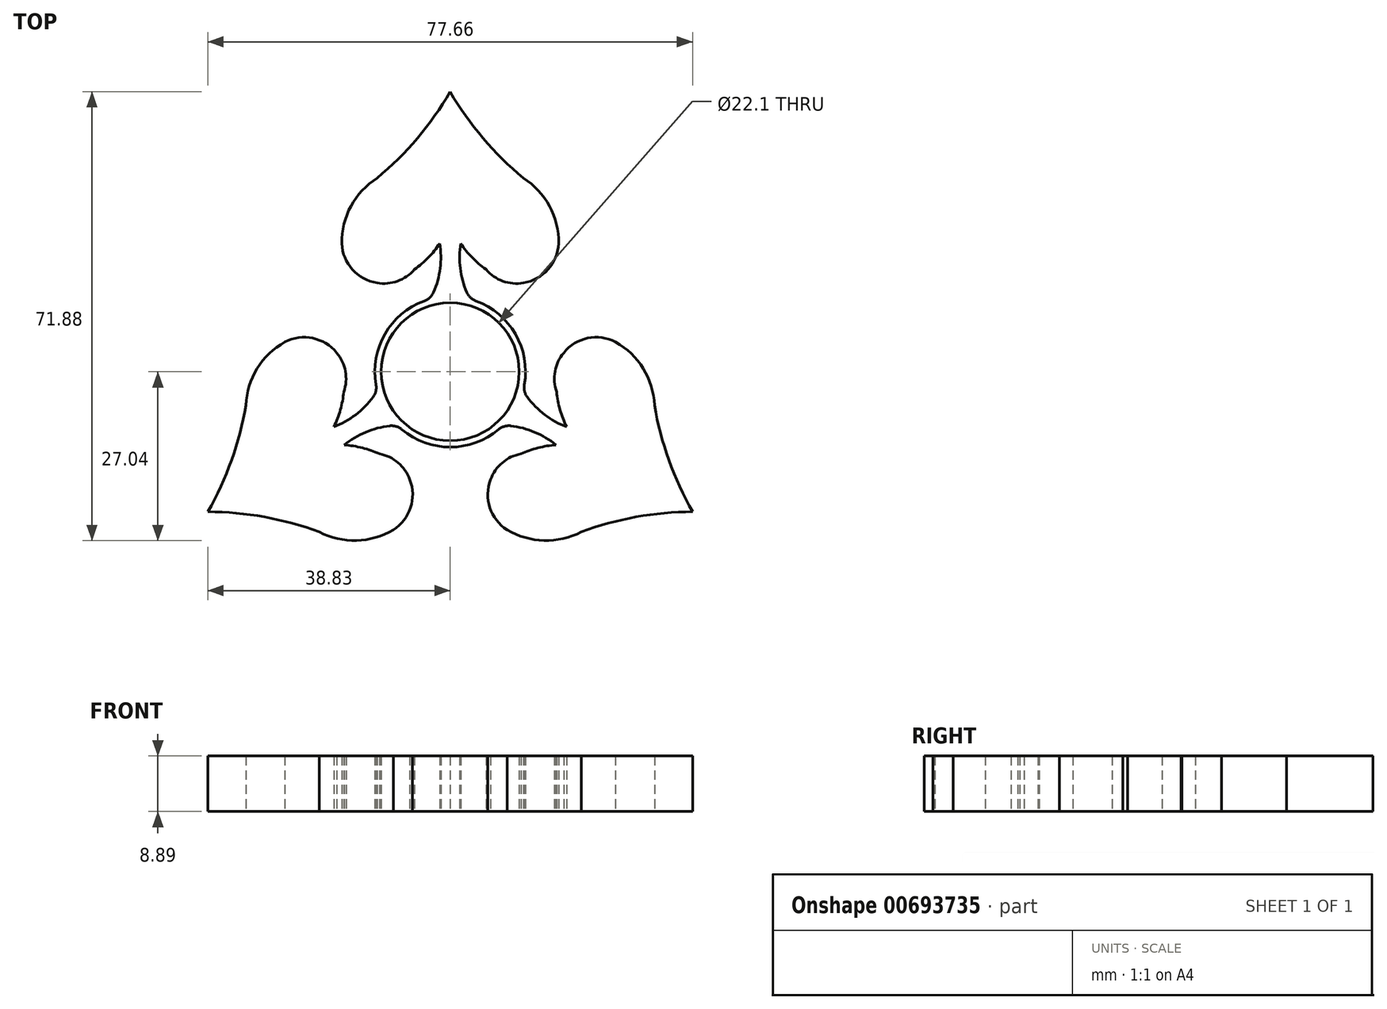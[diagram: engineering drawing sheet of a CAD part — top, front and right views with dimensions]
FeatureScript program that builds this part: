
annotation { "Feature Type Name" : "Feature", "Feature Type Description" : "" }
export const myFeature = defineFeature(function(context is Context, id is Id, definition is map)
    precondition{}
    {
        {
            var Q0;
            Q0=qCreatedBy(makeId("Top.planeOp"),FACE);
            var sketch = newSketch(context, id + "F0", { "sketchPlane" : qUnion([Q0])});
            skArc(sketch, "E0", {"start": v(0, 44.84) * mm, "mid": v(5.25, 37.41) * mm, "end": v(11.71, 31.02) * mm});
            skArc(sketch, "E1", {"start": v(17.37, 20.56) * mm, "mid": v(15.9, 26.52) * mm, "end": v(11.71, 31.02) * mm});
            skArc(sketch, "E2", {"start": v(11.71, 14.23) * mm, "mid": v(15.67, 16.38) * mm, "end": v(17.37, 20.56) * mm});
            skArc(sketch, "E3", {"start": v(5.73, 16.38) * mm, "mid": v(8.44, 14.5) * mm, "end": v(11.71, 14.23) * mm});
            skPoint(sketch, "E3.startSnap0", {"position": v(15.67, 16.38) * mm});
            skArc(sketch, "E4", {"start": v(1.69, 20.56) * mm, "mid": v(3.51, 18.28) * mm, "end": v(5.73, 16.38) * mm});
            skArc(sketch, "E5", {"start": v(1.69, 20.56) * mm, "mid": v(1.6, 16.56) * mm, "end": v(2.67, 12.7) * mm});
            skArc(sketch, "E6.MirrorCS", {"start": v(0, 44.84) * mm, "mid": v(-5.25, 37.41) * mm, "end": v(-11.71, 31.02) * mm});
            skArc(sketch, "E7.MirrorCS", {"start": v(-17.37, 20.56) * mm, "mid": v(-15.9, 26.52) * mm, "end": v(-11.71, 31.02) * mm});
            skArc(sketch, "E8.MirrorCS", {"start": v(-11.71, 14.23) * mm, "mid": v(-15.67, 16.38) * mm, "end": v(-17.37, 20.56) * mm});
            skArc(sketch, "E9.MirrorCS", {"start": v(-5.73, 16.38) * mm, "mid": v(-8.44, 14.5) * mm, "end": v(-11.71, 14.23) * mm});
            skArc(sketch, "E10.MirrorCS", {"start": v(-1.69, 20.56) * mm, "mid": v(-3.51, 18.28) * mm, "end": v(-5.73, 16.38) * mm});
            skArc(sketch, "E11.MirrorCS", {"start": v(-1.69, 20.56) * mm, "mid": v(-1.6, 16.56) * mm, "end": v(-2.67, 12.7) * mm});
            skArc(sketch, "E12.1.0", {"start": v(-18.65, -8.82) * mm, "mid": v(-15.15, -6.89) * mm, "end": v(-12.34, -4.04) * mm});
            skArc(sketch, "E12.1.3", {"start": v(-16.96, -11.74) * mm, "mid": v(-13.54, -9.67) * mm, "end": v(-9.67, -8.66) * mm});
            skArc(sketch, "E12.1.4", {"start": v(-16.96, -11.74) * mm, "mid": v(-14.07, -12.18) * mm, "end": v(-11.32, -13.16) * mm});
            skArc(sketch, "E12.1.5", {"start": v(-11.32, -13.16) * mm, "mid": v(-8.35, -14.56) * mm, "end": v(-6.47, -17.26) * mm});
            skArc(sketch, "E12.1.6", {"start": v(-6.47, -17.26) * mm, "mid": v(-6.35, -21.76) * mm, "end": v(-9.12, -25.32) * mm});
            skArc(sketch, "E12.1.7", {"start": v(-9.12, -25.32) * mm, "mid": v(-15.02, -27.03) * mm, "end": v(-21, -25.65) * mm});
            skArc(sketch, "E12.1.8", {"start": v(-38.83, -22.42) * mm, "mid": v(-29.77, -23.25) * mm, "end": v(-21, -25.65) * mm});
            skArc(sketch, "E12.1.9", {"start": v(-38.83, -22.42) * mm, "mid": v(-35.03, -14.16) * mm, "end": v(-32.72, -5.36) * mm});
            skArc(sketch, "E12.1.10", {"start": v(-26.49, 4.76) * mm, "mid": v(-30.92, 0.51) * mm, "end": v(-32.72, -5.36) * mm});
            skArc(sketch, "E12.1.11", {"start": v(-18.18, 3.03) * mm, "mid": v(-22.02, 5.38) * mm, "end": v(-26.49, 4.76) * mm});
            skArc(sketch, "E12.1.12", {"start": v(-17.05, -3.23) * mm, "mid": v(-16.78, 0.05) * mm, "end": v(-18.18, 3.03) * mm});
            skArc(sketch, "E12.1.13", {"start": v(-18.65, -8.82) * mm, "mid": v(-17.59, -6.1) * mm, "end": v(-17.05, -3.23) * mm});
            skArc(sketch, "E12.2.0", {"start": v(16.96, -11.74) * mm, "mid": v(13.54, -9.67) * mm, "end": v(9.67, -8.66) * mm});
            skArc(sketch, "E12.2.3", {"start": v(18.65, -8.82) * mm, "mid": v(15.15, -6.89) * mm, "end": v(12.34, -4.04) * mm});
            skArc(sketch, "E12.2.4", {"start": v(18.65, -8.82) * mm, "mid": v(17.59, -6.1) * mm, "end": v(17.05, -3.23) * mm});
            skArc(sketch, "E12.2.5", {"start": v(17.05, -3.23) * mm, "mid": v(16.78, 0.05) * mm, "end": v(18.18, 3.03) * mm});
            skArc(sketch, "E12.2.6", {"start": v(18.18, 3.03) * mm, "mid": v(22.02, 5.38) * mm, "end": v(26.49, 4.76) * mm});
            skArc(sketch, "E12.2.7", {"start": v(26.49, 4.76) * mm, "mid": v(30.92, 0.51) * mm, "end": v(32.72, -5.36) * mm});
            skArc(sketch, "E12.2.8", {"start": v(38.83, -22.42) * mm, "mid": v(35.03, -14.16) * mm, "end": v(32.72, -5.36) * mm});
            skArc(sketch, "E12.2.9", {"start": v(38.83, -22.42) * mm, "mid": v(29.77, -23.25) * mm, "end": v(21, -25.65) * mm});
            skArc(sketch, "E12.2.10", {"start": v(9.12, -25.32) * mm, "mid": v(15.02, -27.03) * mm, "end": v(21, -25.65) * mm});
            skArc(sketch, "E12.2.11", {"start": v(6.47, -17.26) * mm, "mid": v(6.35, -21.76) * mm, "end": v(9.12, -25.32) * mm});
            skArc(sketch, "E12.2.12", {"start": v(11.32, -13.16) * mm, "mid": v(8.35, -14.56) * mm, "end": v(6.47, -17.26) * mm});
            skArc(sketch, "E12.2.13", {"start": v(16.96, -11.74) * mm, "mid": v(14.07, -12.18) * mm, "end": v(11.32, -13.16) * mm});
            skCircle(sketch, "E13", {"center": v(0, 0) * mm, "radius": 11.05 * mm});
            skPoint(sketch, "E14.MirrorCS.end.orphan", {"position": v(0, 8.29) * mm});
            skPoint(sketch, "E14.MirrorCS.start.orphan", {"position": v(-5.73, 8.29) * mm});
            skArc(sketch, "E15", {"start": v(8.48, -8.58) * mm, "mid": v(11.79, 2.58) * mm, "end": v(4.13, 11.34) * mm});
            skArc(sketch, "E16", {"start": v(-8.48, -8.58) * mm, "mid": v(0, -12.07) * mm, "end": v(8.48, -8.58) * mm});
            skArc(sketch, "E17", {"start": v(-11.67, -3.05) * mm, "mid": v(-10.45, -6.03) * mm, "end": v(-8.48, -8.58) * mm});
            skArc(sketch, "E18", {"start": v(-4.13, 11.34) * mm, "mid": v(-10.69, 5.6) * mm, "end": v(-11.67, -3.05) * mm});
            skPoint(sketch, "E19.end.orphan", {"position": v(5.73, 8.29) * mm});
            skPoint(sketch, "E20.orphan", {"position": v(-4.31, -9.1) * mm});
            skPoint(sketch, "E21.orphan", {"position": v(-10.04, 0.82) * mm});
            skArc(sketch, "E22.filletArc", {"start": v(2.67, 12.7) * mm, "mid": v(3.26, 11.87) * mm, "end": v(4.13, 11.34) * mm});
            skPoint(sketch, "E23.visualSharp", {"position": v(-3.2, 11.63) * mm});
            skArc(sketch, "E23.filletArc", {"start": v(-4.13, 11.34) * mm, "mid": v(-3.26, 11.87) * mm, "end": v(-2.67, 12.7) * mm});
            skArc(sketch, "E24.1.0", {"start": v(-12.34, -4.04) * mm, "mid": v(-11.91, -3.12) * mm, "end": v(-11.88, -2.1) * mm});
            skArc(sketch, "E24.1.1", {"start": v(-7.75, -9.24) * mm, "mid": v(-8.65, -8.76) * mm, "end": v(-9.67, -8.66) * mm});
            skArc(sketch, "E24.2.0", {"start": v(9.67, -8.66) * mm, "mid": v(8.65, -8.76) * mm, "end": v(7.75, -9.24) * mm});
            skArc(sketch, "E24.2.1", {"start": v(11.88, -2.1) * mm, "mid": v(11.91, -3.12) * mm, "end": v(12.34, -4.04) * mm});
            skSolve(sketch);
        }
        {
            var Q0;
            {var subQ0=sQuery(id+"F0.wireOp",EDGE,"E6.MirrorCS");var subQ1=sQuery(id+"F0.wireOp",EDGE,"E0");var subQ2=makeQuery(id+"F0.imprint","INTERSECT",VERTEX,{"derivedFrom":[subQ1,subQ0]});Q0=makeQuery(id+"F0.imprint","IMPRINT",FACE,{"disambiguationData":[TD([[makeQuery(id+"F0.imprint","IMPRINT",EDGE,{"disambiguationData":[TD([[subQ2,-1.0]])],"derivedFrom":subQ1}),-1.0]])]});}
            var Q1;
            {var subQ0=sQuery(id+"F0.wireOp",EDGE,"E1");var subQ1=sQuery(id+"F0.wireOp",EDGE,"E0");var subQ2=makeQuery(id+"F0.imprint","INTERSECT",VERTEX,{"derivedFrom":[subQ1,subQ0]});Q1=makeQuery(id+"F0.imprint","IMPRINT",FACE,{"disambiguationData":[TD([[makeQuery(id+"F0.imprint","IMPRINT",EDGE,{"disambiguationData":[TD([[subQ2,1.0]])],"derivedFrom":subQ1}),1.0]])]});}
            var Q2;
            {var subQ0=sQuery(id+"F0.wireOp",EDGE,"E5");var subQ1=sQuery(id+"F0.wireOp",EDGE,"E4");var subQ2=makeQuery(id+"F0.imprint","INTERSECT",VERTEX,{"derivedFrom":[subQ1,subQ0]});Q2=makeQuery(id+"F0.imprint","IMPRINT",FACE,{"disambiguationData":[TD([[makeQuery(id+"F0.imprint","IMPRINT",EDGE,{"disambiguationData":[TD([[subQ2,-1.0]])],"derivedFrom":subQ1}),-1.0]])]});}
            var Q3;
            {var subQ0=sQuery(id+"F0.wireOp",EDGE,"E7.MirrorCS");var subQ1=sQuery(id+"F0.wireOp",EDGE,"E6.MirrorCS");var subQ2=makeQuery(id+"F0.imprint","INTERSECT",VERTEX,{"derivedFrom":[subQ1,subQ0]});Q3=makeQuery(id+"F0.imprint","IMPRINT",FACE,{"disambiguationData":[TD([[makeQuery(id+"F0.imprint","IMPRINT",EDGE,{"disambiguationData":[TD([[subQ2,1.0]])],"derivedFrom":subQ1}),-1.0]])]});}
            var Q4;
            {var subQ1=sQuery(id+"F0.wireOp",EDGE,"E8.MirrorCS");Q4=makeQuery(id+"F0.imprint","IMPRINT",FACE,{"disambiguationData":[TD([[makeQuery(id+"F0.imprint","IMPRINT",EDGE,{"derivedFrom":subQ1}),-1.0]])]});}
            var Q5;
            {var subQ0=sQuery(id+"F0.wireOp",EDGE,"E11.MirrorCS");var subQ1=sQuery(id+"F0.wireOp",EDGE,"E10.MirrorCS");var subQ2=makeQuery(id+"F0.imprint","INTERSECT",VERTEX,{"derivedFrom":[subQ1,subQ0]});Q5=makeQuery(id+"F0.imprint","IMPRINT",FACE,{"disambiguationData":[TD([[makeQuery(id+"F0.imprint","IMPRINT",EDGE,{"disambiguationData":[TD([[subQ2,-1.0]])],"derivedFrom":subQ1}),1.0]])]});}
            var Q6;
            {var subQ0=sQuery(id+"F0.wireOp",EDGE,"E12.1.13");var subQ1=sQuery(id+"F0.wireOp",EDGE,"E12.1.0");var subQ2=makeQuery(id+"F0.imprint","INTERSECT",VERTEX,{"derivedFrom":[subQ1,subQ0]});Q6=makeQuery(id+"F0.imprint","IMPRINT",FACE,{"disambiguationData":[TD([[makeQuery(id+"F0.imprint","IMPRINT",EDGE,{"disambiguationData":[TD([[subQ2,-1.0]])],"derivedFrom":subQ1}),1.0]])]});}
            var Q7;
            {var subQ0=sQuery(id+"F0.wireOp",EDGE,"E12.1.4");var subQ1=sQuery(id+"F0.wireOp",EDGE,"E12.1.3");var subQ2=makeQuery(id+"F0.imprint","INTERSECT",VERTEX,{"derivedFrom":[subQ1,subQ0]});Q7=makeQuery(id+"F0.imprint","IMPRINT",FACE,{"disambiguationData":[TD([[makeQuery(id+"F0.imprint","IMPRINT",EDGE,{"disambiguationData":[TD([[subQ2,-1.0]])],"derivedFrom":subQ1}),-1.0]])]});}
            var Q8;
            {var subQ4=sQuery(id+"F0.wireOp",EDGE,"E12.1.5");Q8=makeQuery(id+"F0.imprint","IMPRINT",FACE,{"disambiguationData":[TD([[makeQuery(id+"F0.imprint","IMPRINT",EDGE,{"derivedFrom":subQ4}),-1.0]])]});}
            var Q9;
            {var subQ0=sQuery(id+"F0.wireOp",EDGE,"E12.1.8");var subQ1=sQuery(id+"F0.wireOp",EDGE,"E12.1.7");var subQ2=makeQuery(id+"F0.imprint","INTERSECT",VERTEX,{"derivedFrom":[subQ1,subQ0]});Q9=makeQuery(id+"F0.imprint","IMPRINT",FACE,{"disambiguationData":[TD([[makeQuery(id+"F0.imprint","IMPRINT",EDGE,{"disambiguationData":[TD([[subQ2,1.0]])],"derivedFrom":subQ1}),1.0]])]});}
            var Q10;
            {var subQ0=sQuery(id+"F0.wireOp",EDGE,"E12.1.9");var subQ1=sQuery(id+"F0.wireOp",EDGE,"E12.1.8");var subQ2=makeQuery(id+"F0.imprint","INTERSECT",VERTEX,{"derivedFrom":[subQ1,subQ0]});Q10=makeQuery(id+"F0.imprint","IMPRINT",FACE,{"disambiguationData":[TD([[makeQuery(id+"F0.imprint","IMPRINT",EDGE,{"disambiguationData":[TD([[subQ2,-1.0]])],"derivedFrom":subQ1}),1.0]])]});}
            var Q11;
            {var subQ0=sQuery(id+"F0.wireOp",EDGE,"E12.1.10");var subQ1=sQuery(id+"F0.wireOp",EDGE,"E12.1.9");var subQ2=makeQuery(id+"F0.imprint","INTERSECT",VERTEX,{"derivedFrom":[subQ1,subQ0]});Q11=makeQuery(id+"F0.imprint","IMPRINT",FACE,{"disambiguationData":[TD([[makeQuery(id+"F0.imprint","IMPRINT",EDGE,{"disambiguationData":[TD([[subQ2,1.0]])],"derivedFrom":subQ1}),1.0]])]});}
            var Q12;
            {var subQ1=sQuery(id+"F0.wireOp",EDGE,"E12.1.11");Q12=makeQuery(id+"F0.imprint","IMPRINT",FACE,{"disambiguationData":[TD([[makeQuery(id+"F0.imprint","IMPRINT",EDGE,{"derivedFrom":subQ1}),1.0]])]});}
            var Q13;
            {var subQ0=sQuery(id+"F0.wireOp",EDGE,"E12.2.13");var subQ1=sQuery(id+"F0.wireOp",EDGE,"E12.2.0");var subQ2=makeQuery(id+"F0.imprint","INTERSECT",VERTEX,{"derivedFrom":[subQ1,subQ0]});Q13=makeQuery(id+"F0.imprint","IMPRINT",FACE,{"disambiguationData":[TD([[makeQuery(id+"F0.imprint","IMPRINT",EDGE,{"disambiguationData":[TD([[subQ2,-1.0]])],"derivedFrom":subQ1}),1.0]])]});}
            var Q14;
            {var subQ0=sQuery(id+"F0.wireOp",EDGE,"E12.2.4");var subQ1=sQuery(id+"F0.wireOp",EDGE,"E12.2.3");var subQ2=makeQuery(id+"F0.imprint","INTERSECT",VERTEX,{"derivedFrom":[subQ1,subQ0]});Q14=makeQuery(id+"F0.imprint","IMPRINT",FACE,{"disambiguationData":[TD([[makeQuery(id+"F0.imprint","IMPRINT",EDGE,{"disambiguationData":[TD([[subQ2,-1.0]])],"derivedFrom":subQ1}),-1.0]])]});}
            var Q15;
            {var subQ4=sQuery(id+"F0.wireOp",EDGE,"E12.2.5");Q15=makeQuery(id+"F0.imprint","IMPRINT",FACE,{"disambiguationData":[TD([[makeQuery(id+"F0.imprint","IMPRINT",EDGE,{"derivedFrom":subQ4}),-1.0]])]});}
            var Q16;
            {var subQ0=sQuery(id+"F0.wireOp",EDGE,"E12.2.8");var subQ1=sQuery(id+"F0.wireOp",EDGE,"E12.2.7");var subQ2=makeQuery(id+"F0.imprint","INTERSECT",VERTEX,{"derivedFrom":[subQ1,subQ0]});Q16=makeQuery(id+"F0.imprint","IMPRINT",FACE,{"disambiguationData":[TD([[makeQuery(id+"F0.imprint","IMPRINT",EDGE,{"disambiguationData":[TD([[subQ2,1.0]])],"derivedFrom":subQ1}),1.0]])]});}
            var Q17;
            {var subQ0=sQuery(id+"F0.wireOp",EDGE,"E12.2.9");var subQ1=sQuery(id+"F0.wireOp",EDGE,"E12.2.8");var subQ2=makeQuery(id+"F0.imprint","INTERSECT",VERTEX,{"derivedFrom":[subQ1,subQ0]});Q17=makeQuery(id+"F0.imprint","IMPRINT",FACE,{"disambiguationData":[TD([[makeQuery(id+"F0.imprint","IMPRINT",EDGE,{"disambiguationData":[TD([[subQ2,-1.0]])],"derivedFrom":subQ1}),1.0]])]});}
            var Q18;
            {var subQ0=sQuery(id+"F0.wireOp",EDGE,"E12.2.10");var subQ1=sQuery(id+"F0.wireOp",EDGE,"E12.2.9");var subQ2=makeQuery(id+"F0.imprint","INTERSECT",VERTEX,{"derivedFrom":[subQ1,subQ0]});Q18=makeQuery(id+"F0.imprint","IMPRINT",FACE,{"disambiguationData":[TD([[makeQuery(id+"F0.imprint","IMPRINT",EDGE,{"disambiguationData":[TD([[subQ2,1.0]])],"derivedFrom":subQ1}),1.0]])]});}
            var Q19;
            {var subQ1=sQuery(id+"F0.wireOp",EDGE,"E12.2.11");Q19=makeQuery(id+"F0.imprint","IMPRINT",FACE,{"disambiguationData":[TD([[makeQuery(id+"F0.imprint","IMPRINT",EDGE,{"derivedFrom":subQ1}),1.0]])]});}
            var Q20;
            {var subQ0=sQuery(id+"F0.wireOp",EDGE,"E17");Q20=makeQuery(id+"F0.imprint","IMPRINT",FACE,{"disambiguationData":[TD([[makeQuery(id+"F0.imprint","IMPRINT",EDGE,{"derivedFrom":subQ0}),-1.0]])]});}
            var Q21;
            {var subQ3=sQuery(id+"F0.wireOp",EDGE,"E24.2.0");Q21=makeQuery(id+"F0.imprint","IMPRINT",FACE,{"disambiguationData":[TD([[makeQuery(id+"F0.imprint","IMPRINT",EDGE,{"derivedFrom":subQ3}),-1.0]])]});}
            var Q22;
            Q22=makeQuery(id+"F0.imprint","IMPRINT",FACE,{"disambiguationData":[TD([[makeQuery(id+"F0.imprint","IMPRINT",EDGE,{"derivedFrom":sQuery(id+"F0.wireOp",EDGE,"E13")}),-1.0]])]});
            var Q23;
            {var subQ1=sQuery(id+"F0.wireOp",EDGE,"E0");var subQ5=sQuery(id+"F0.wireOp",EDGE,"E1");var subQ6=makeQuery(id+"F0.imprint","INTERSECT",VERTEX,{"derivedFrom":[subQ1,subQ5]});Q23=makeQuery(id+"F0.imprint","IMPRINT",FACE,{"disambiguationData":[TD([[makeQuery(id+"F0.imprint","IMPRINT",EDGE,{"disambiguationData":[TD([[subQ6,1.0]])],"derivedFrom":subQ1}),-1.0]])]});}
            var Q24;
            {var subQ0=sQuery(id+"F0.wireOp",EDGE,"E12.1.13");var subQ1=sQuery(id+"F0.wireOp",EDGE,"E12.1.0");var subQ2=makeQuery(id+"F0.imprint","INTERSECT",VERTEX,{"derivedFrom":[subQ1,subQ0]});Q24=makeQuery(id+"F0.imprint","IMPRINT",FACE,{"disambiguationData":[TD([[makeQuery(id+"F0.imprint","IMPRINT",EDGE,{"disambiguationData":[TD([[subQ2,-1.0]])],"derivedFrom":subQ1}),-1.0]])]});}
            var Q25;
            {var subQ9=sQuery(id+"F0.wireOp",EDGE,"E12.2.13");var subQ10=sQuery(id+"F0.wireOp",EDGE,"E12.2.0");var subQ11=makeQuery(id+"F0.imprint","INTERSECT",VERTEX,{"derivedFrom":[subQ10,subQ9]});Q25=makeQuery(id+"F0.imprint","IMPRINT",FACE,{"disambiguationData":[TD([[makeQuery(id+"F0.imprint","IMPRINT",EDGE,{"disambiguationData":[TD([[subQ11,-1.0]])],"derivedFrom":subQ10}),-1.0]])]});}
            var Q26;
            {var subQ1=sQuery(id+"F0.wireOp",EDGE,"E2");Q26=makeQuery(id+"F0.imprint","IMPRINT",FACE,{"disambiguationData":[TD([[makeQuery(id+"F0.imprint","IMPRINT",EDGE,{"derivedFrom":subQ1}),1.0]])]});}
            extrude(context, id + "F1", {"entities" : qUnion([Q0, Q1, Q2, Q3, Q4, Q5, Q6, Q7, Q8, Q9, Q10, Q11, Q12, Q13, Q14, Q15, Q16, Q17, Q18, Q19, Q20, Q21, Q22, Q23, Q24, Q25, Q26]), "depth" : 8.9 * mm, "offsetDistance" : 25.4 * mm});
        }
    });
